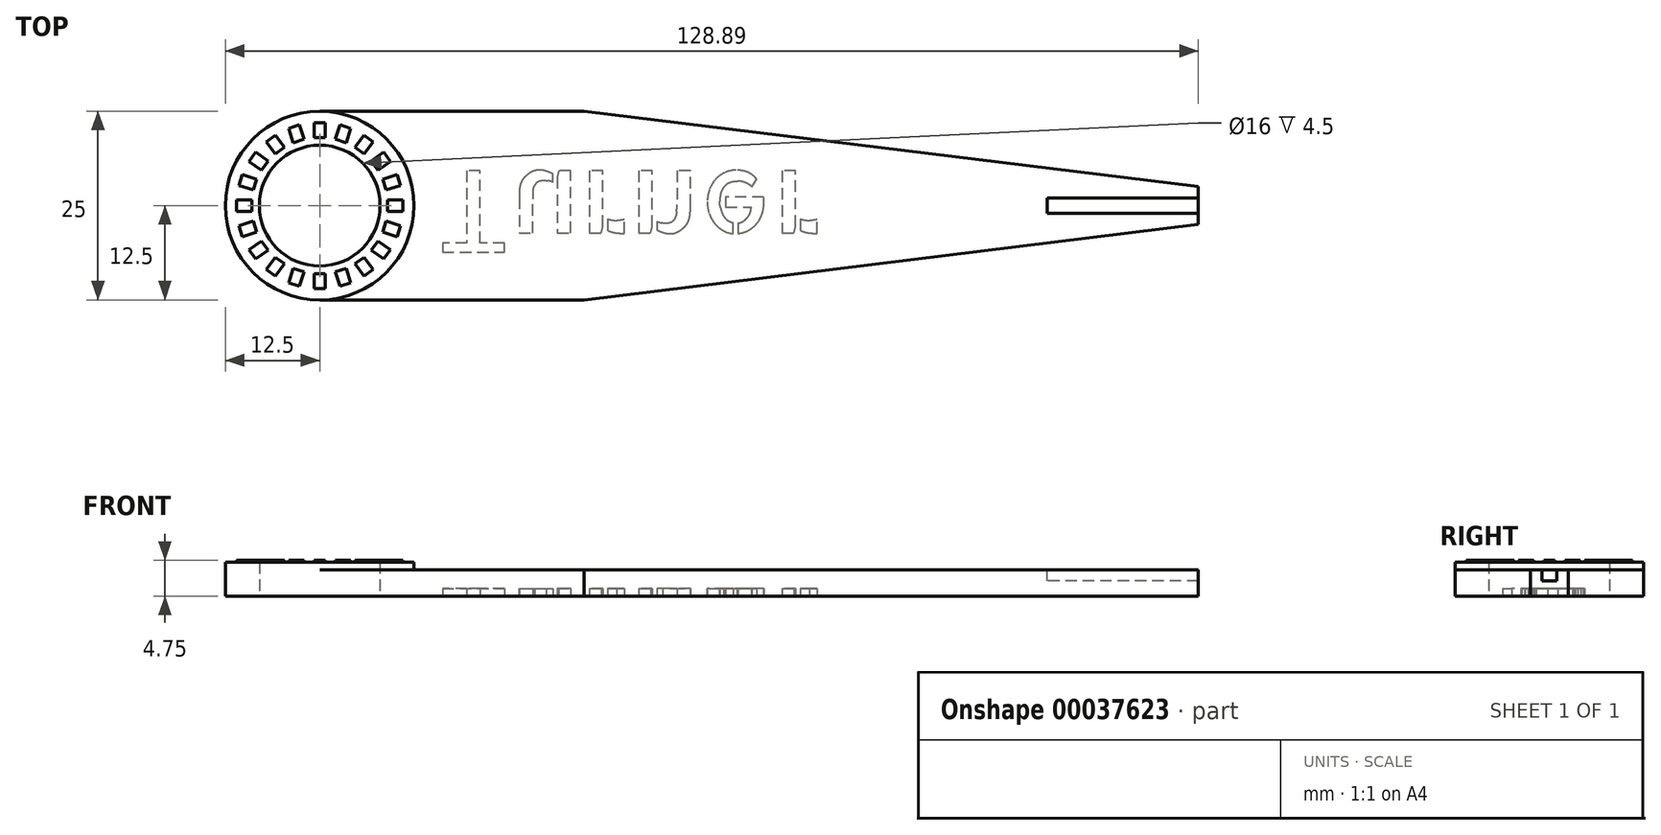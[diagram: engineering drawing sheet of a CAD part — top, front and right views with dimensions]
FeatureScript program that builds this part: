
annotation { "Feature Type Name" : "Feature", "Feature Type Description" : "" }
export const myFeature = defineFeature(function(context is Context, id is Id, definition is map)
    precondition{}
    {
        {
            var Q0;
            Q0=qCreatedBy(makeId("Top.planeOp"),FACE);
            var sketch = newSketch(context, id + "F0", { "sketchPlane" : qUnion([Q0])});
            skCircle(sketch, "E0", {"center": v(0, 0) * mm, "radius": 8 * mm});
            skCircle(sketch, "E1", {"center": v(0, 0) * mm, "radius": 12.5 * mm});
            skLineSegment(sketch, "E2", {"start": v(0, 12.5) * mm, "end": v(35, 12.5) * mm});
            skPoint(sketch, "E3", {"position": v(0, 12.5) * mm});
            skLineSegment(sketch, "E4", {"start": v(0, 0) * mm, "end": v(40.63, 0) * mm, "construction": true});
            skLineSegment(sketch, "E5.MirrorCS", {"start": v(0, -12.5) * mm, "end": v(35, -12.5) * mm});
            skLineSegment(sketch, "E6", {"start": v(35, 12.5) * mm, "end": v(108.8, 12.5) * mm, "construction": true});
            skLineSegment(sketch, "E7", {"start": v(35, 12.5) * mm, "end": v(116.39, 2.5) * mm});
            skLineSegment(sketch, "E8.MirrorCS", {"start": v(35, -12.5) * mm, "end": v(116.39, -2.5) * mm});
            skLineSegment(sketch, "E9", {"start": v(116.39, 2.5) * mm, "end": v(116.39, -2.5) * mm});
            skSolve(sketch);
        }
        {
            var Q0;
            Q0 = qSketchRegion(id + "F0", true);
            extrude(context, id + "F1", {"entities" : qUnion([Q0]), "depth" : 3.5 * mm});
        }
        {
            var Q0;
            Q0=makeQuery(id+"F1.opExtrude","CAP_FACE",FACE,{"disambiguationData":[OSD([sQuery(id+"F0.wireOp",EDGE,"E0"),sQuery(id+"F0.wireOp",EDGE,"E1"),sQuery(id+"F0.wireOp",EDGE,"E2"),sQuery(id+"F0.wireOp",EDGE,"E5.MirrorCS"),sQuery(id+"F0.wireOp",EDGE,"E7"),sQuery(id+"F0.wireOp",EDGE,"E8.MirrorCS"),sQuery(id+"F0.wireOp",EDGE,"E9")])],"isStart":false});
            var sketch = newSketch(context, id + "F2", { "sketchPlane" : qUnion([Q0])});
            skCircle(sketch, "E10", {"center": v(0, 0) * mm, "radius": 12.5 * mm});
            skCircle(sketch, "E11", {"center": v(0, 0) * mm, "radius": 8 * mm});
            skSolve(sketch);
        }
        {
            var Q0;
            Q0 = qSketchRegion(id + "F2", true);
            extrude(context, id + "F3", {"entities" : qUnion([Q0]), "operationType" : NewBodyOperationType.ADD, "depth" : 1 * mm});
        }
        {
            var Q0;
            Q0=makeQuery(id+"F3.opExtrude","CAP_FACE",FACE,{"disambiguationData":[OSD([sQuery(id+"F2.wireOp",EDGE,"E10"),sQuery(id+"F2.wireOp",EDGE,"E11")])],"isStart":false});
            var sketch = newSketch(context, id + "F4", { "sketchPlane" : qUnion([Q0])});
            skLineSegment(sketch, "E12.bottom", {"start": v(-0.75, 11) * mm, "end": v(0.75, 11) * mm});
            skLineSegment(sketch, "E12.top", {"start": v(-0.75, 9) * mm, "end": v(0.75, 9) * mm});
            skLineSegment(sketch, "E12.left", {"start": v(-0.75, 11) * mm, "end": v(-0.75, 9) * mm});
            skLineSegment(sketch, "E12.right", {"start": v(0.75, 11) * mm, "end": v(0.75, 9) * mm});
            skPoint(sketch, "E13", {"position": v(0, 8) * mm});
            skLineSegment(sketch, "E14.1.0", {"start": v(-4.11, 10.23) * mm, "end": v(-2.69, 10.7) * mm});
            skLineSegment(sketch, "E14.1.1", {"start": v(-4.11, 10.23) * mm, "end": v(-3.5, 8.33) * mm});
            skLineSegment(sketch, "E14.1.2", {"start": v(-3.5, 8.33) * mm, "end": v(-2.07, 8.8) * mm});
            skLineSegment(sketch, "E14.1.3", {"start": v(-2.69, 10.7) * mm, "end": v(-2.07, 8.8) * mm});
            skLineSegment(sketch, "E14.2.0", {"start": v(-7.07, 8.46) * mm, "end": v(-5.86, 9.34) * mm});
            skLineSegment(sketch, "E14.2.1", {"start": v(-7.07, 8.46) * mm, "end": v(-5.9, 6.84) * mm});
            skLineSegment(sketch, "E14.2.2", {"start": v(-5.9, 6.84) * mm, "end": v(-4.68, 7.72) * mm});
            skLineSegment(sketch, "E14.2.3", {"start": v(-5.86, 9.34) * mm, "end": v(-4.68, 7.72) * mm});
            skLineSegment(sketch, "E14.3.0", {"start": v(-9.34, 5.86) * mm, "end": v(-8.46, 7.07) * mm});
            skLineSegment(sketch, "E14.3.1", {"start": v(-9.34, 5.86) * mm, "end": v(-7.72, 4.68) * mm});
            skLineSegment(sketch, "E14.3.2", {"start": v(-7.72, 4.68) * mm, "end": v(-6.84, 5.9) * mm});
            skLineSegment(sketch, "E14.3.3", {"start": v(-8.46, 7.07) * mm, "end": v(-6.84, 5.9) * mm});
            skLineSegment(sketch, "E14.4.0", {"start": v(-10.7, 2.69) * mm, "end": v(-10.23, 4.11) * mm});
            skLineSegment(sketch, "E14.4.1", {"start": v(-10.7, 2.69) * mm, "end": v(-8.8, 2.07) * mm});
            skLineSegment(sketch, "E14.4.2", {"start": v(-8.8, 2.07) * mm, "end": v(-8.33, 3.5) * mm});
            skLineSegment(sketch, "E14.4.3", {"start": v(-10.23, 4.11) * mm, "end": v(-8.33, 3.5) * mm});
            skLineSegment(sketch, "E14.5.0", {"start": v(-11, -0.75) * mm, "end": v(-11, 0.75) * mm});
            skLineSegment(sketch, "E14.5.1", {"start": v(-11, -0.75) * mm, "end": v(-9, -0.75) * mm});
            skLineSegment(sketch, "E14.5.2", {"start": v(-9, -0.75) * mm, "end": v(-9, 0.75) * mm});
            skLineSegment(sketch, "E14.5.3", {"start": v(-11, 0.75) * mm, "end": v(-9, 0.75) * mm});
            skLineSegment(sketch, "E14.6.0", {"start": v(-10.23, -4.11) * mm, "end": v(-10.7, -2.69) * mm});
            skLineSegment(sketch, "E14.6.1", {"start": v(-10.23, -4.11) * mm, "end": v(-8.33, -3.5) * mm});
            skLineSegment(sketch, "E14.6.2", {"start": v(-8.33, -3.5) * mm, "end": v(-8.8, -2.07) * mm});
            skLineSegment(sketch, "E14.6.3", {"start": v(-10.7, -2.69) * mm, "end": v(-8.8, -2.07) * mm});
            skLineSegment(sketch, "E14.7.0", {"start": v(-8.46, -7.07) * mm, "end": v(-9.34, -5.86) * mm});
            skLineSegment(sketch, "E14.7.1", {"start": v(-8.46, -7.07) * mm, "end": v(-6.84, -5.9) * mm});
            skLineSegment(sketch, "E14.7.2", {"start": v(-6.84, -5.9) * mm, "end": v(-7.72, -4.68) * mm});
            skLineSegment(sketch, "E14.7.3", {"start": v(-9.34, -5.86) * mm, "end": v(-7.72, -4.68) * mm});
            skLineSegment(sketch, "E14.8.0", {"start": v(-5.86, -9.34) * mm, "end": v(-7.07, -8.46) * mm});
            skLineSegment(sketch, "E14.8.1", {"start": v(-5.86, -9.34) * mm, "end": v(-4.68, -7.72) * mm});
            skLineSegment(sketch, "E14.8.2", {"start": v(-4.68, -7.72) * mm, "end": v(-5.9, -6.84) * mm});
            skLineSegment(sketch, "E14.8.3", {"start": v(-7.07, -8.46) * mm, "end": v(-5.9, -6.84) * mm});
            skLineSegment(sketch, "E14.9.0", {"start": v(-2.69, -10.7) * mm, "end": v(-4.11, -10.23) * mm});
            skLineSegment(sketch, "E14.9.1", {"start": v(-2.69, -10.7) * mm, "end": v(-2.07, -8.8) * mm});
            skLineSegment(sketch, "E14.9.2", {"start": v(-2.07, -8.8) * mm, "end": v(-3.5, -8.33) * mm});
            skLineSegment(sketch, "E14.9.3", {"start": v(-4.11, -10.23) * mm, "end": v(-3.5, -8.33) * mm});
            skLineSegment(sketch, "E14.10.0", {"start": v(0.75, -11) * mm, "end": v(-0.75, -11) * mm});
            skLineSegment(sketch, "E14.10.1", {"start": v(0.75, -11) * mm, "end": v(0.75, -9) * mm});
            skLineSegment(sketch, "E14.10.2", {"start": v(0.75, -9) * mm, "end": v(-0.75, -9) * mm});
            skLineSegment(sketch, "E14.10.3", {"start": v(-0.75, -11) * mm, "end": v(-0.75, -9) * mm});
            skLineSegment(sketch, "E14.11.0", {"start": v(4.11, -10.23) * mm, "end": v(2.69, -10.7) * mm});
            skLineSegment(sketch, "E14.11.1", {"start": v(4.11, -10.23) * mm, "end": v(3.5, -8.33) * mm});
            skLineSegment(sketch, "E14.11.2", {"start": v(3.5, -8.33) * mm, "end": v(2.07, -8.8) * mm});
            skLineSegment(sketch, "E14.11.3", {"start": v(2.69, -10.7) * mm, "end": v(2.07, -8.8) * mm});
            skLineSegment(sketch, "E14.12.0", {"start": v(7.07, -8.46) * mm, "end": v(5.86, -9.34) * mm});
            skLineSegment(sketch, "E14.12.1", {"start": v(7.07, -8.46) * mm, "end": v(5.9, -6.84) * mm});
            skLineSegment(sketch, "E14.12.2", {"start": v(5.9, -6.84) * mm, "end": v(4.68, -7.72) * mm});
            skLineSegment(sketch, "E14.12.3", {"start": v(5.86, -9.34) * mm, "end": v(4.68, -7.72) * mm});
            skLineSegment(sketch, "E14.13.0", {"start": v(9.34, -5.86) * mm, "end": v(8.46, -7.07) * mm});
            skLineSegment(sketch, "E14.13.1", {"start": v(9.34, -5.86) * mm, "end": v(7.72, -4.68) * mm});
            skLineSegment(sketch, "E14.13.2", {"start": v(7.72, -4.68) * mm, "end": v(6.84, -5.9) * mm});
            skLineSegment(sketch, "E14.13.3", {"start": v(8.46, -7.07) * mm, "end": v(6.84, -5.9) * mm});
            skLineSegment(sketch, "E14.14.0", {"start": v(10.7, -2.69) * mm, "end": v(10.23, -4.11) * mm});
            skLineSegment(sketch, "E14.14.1", {"start": v(10.7, -2.69) * mm, "end": v(8.8, -2.07) * mm});
            skLineSegment(sketch, "E14.14.2", {"start": v(8.8, -2.07) * mm, "end": v(8.33, -3.5) * mm});
            skLineSegment(sketch, "E14.14.3", {"start": v(10.23, -4.11) * mm, "end": v(8.33, -3.5) * mm});
            skLineSegment(sketch, "E14.15.0", {"start": v(11, 0.75) * mm, "end": v(11, -0.75) * mm});
            skLineSegment(sketch, "E14.15.1", {"start": v(11, 0.75) * mm, "end": v(9, 0.75) * mm});
            skLineSegment(sketch, "E14.15.2", {"start": v(9, 0.75) * mm, "end": v(9, -0.75) * mm});
            skLineSegment(sketch, "E14.15.3", {"start": v(11, -0.75) * mm, "end": v(9, -0.75) * mm});
            skLineSegment(sketch, "E14.16.0", {"start": v(10.23, 4.11) * mm, "end": v(10.7, 2.69) * mm});
            skLineSegment(sketch, "E14.16.1", {"start": v(10.23, 4.11) * mm, "end": v(8.33, 3.5) * mm});
            skLineSegment(sketch, "E14.16.2", {"start": v(8.33, 3.5) * mm, "end": v(8.8, 2.07) * mm});
            skLineSegment(sketch, "E14.16.3", {"start": v(10.7, 2.69) * mm, "end": v(8.8, 2.07) * mm});
            skLineSegment(sketch, "E14.17.0", {"start": v(8.46, 7.07) * mm, "end": v(9.34, 5.86) * mm});
            skLineSegment(sketch, "E14.17.1", {"start": v(8.46, 7.07) * mm, "end": v(6.84, 5.9) * mm});
            skLineSegment(sketch, "E14.17.2", {"start": v(6.84, 5.9) * mm, "end": v(7.72, 4.68) * mm});
            skLineSegment(sketch, "E14.17.3", {"start": v(9.34, 5.86) * mm, "end": v(7.72, 4.68) * mm});
            skLineSegment(sketch, "E14.18.0", {"start": v(5.86, 9.34) * mm, "end": v(7.07, 8.46) * mm});
            skLineSegment(sketch, "E14.18.1", {"start": v(5.86, 9.34) * mm, "end": v(4.68, 7.72) * mm});
            skLineSegment(sketch, "E14.18.2", {"start": v(4.68, 7.72) * mm, "end": v(5.9, 6.84) * mm});
            skLineSegment(sketch, "E14.18.3", {"start": v(7.07, 8.46) * mm, "end": v(5.9, 6.84) * mm});
            skLineSegment(sketch, "E14.19.0", {"start": v(2.69, 10.7) * mm, "end": v(4.11, 10.23) * mm});
            skLineSegment(sketch, "E14.19.1", {"start": v(2.69, 10.7) * mm, "end": v(2.07, 8.8) * mm});
            skLineSegment(sketch, "E14.19.2", {"start": v(2.07, 8.8) * mm, "end": v(3.5, 8.33) * mm});
            skLineSegment(sketch, "E14.19.3", {"start": v(4.11, 10.23) * mm, "end": v(3.5, 8.33) * mm});
            skPoint(sketch, "E14.center", {"position": v(0, 0) * mm});
            skSolve(sketch);
        }
        {
            var Q0;
            Q0 = qSketchRegion(id + "F4", true);
            extrude(context, id + "F5", {"entities" : qUnion([Q0]), "operationType" : NewBodyOperationType.ADD, "depth" : .25 * mm});
        }
        {
            var Q0;
            Q0=makeQuery(id+"F1.opExtrude","CAP_FACE",FACE,{"disambiguationData":[OSD([sQuery(id+"F0.wireOp",EDGE,"E0"),sQuery(id+"F0.wireOp",EDGE,"E1"),sQuery(id+"F0.wireOp",EDGE,"E2"),sQuery(id+"F0.wireOp",EDGE,"E5.MirrorCS"),sQuery(id+"F0.wireOp",EDGE,"E7"),sQuery(id+"F0.wireOp",EDGE,"E8.MirrorCS"),sQuery(id+"F0.wireOp",EDGE,"E9")])],"isStart":false});
            var sketch = newSketch(context, id + "F6", { "sketchPlane" : qUnion([Q0])});
            skLineSegment(sketch, "E15.bottom", {"start": v(116.39, 1) * mm, "end": v(96.39, 1) * mm});
            skLineSegment(sketch, "E15.top", {"start": v(116.39, -1) * mm, "end": v(96.39, -1) * mm});
            skLineSegment(sketch, "E15.left", {"start": v(116.39, 1) * mm, "end": v(116.39, -1) * mm});
            skLineSegment(sketch, "E15.right", {"start": v(96.39, 1) * mm, "end": v(96.39, -1) * mm});
            skSolve(sketch);
        }
        {
            var Q0;
            Q0=makeQuery(id+"F1.opExtrude","CAP_FACE",FACE,{"disambiguationData":[OSD([sQuery(id+"F0.wireOp",EDGE,"E0"),sQuery(id+"F0.wireOp",EDGE,"E1"),sQuery(id+"F0.wireOp",EDGE,"E2"),sQuery(id+"F0.wireOp",EDGE,"E5.MirrorCS"),sQuery(id+"F0.wireOp",EDGE,"E7"),sQuery(id+"F0.wireOp",EDGE,"E8.MirrorCS"),sQuery(id+"F0.wireOp",EDGE,"E9")])],"isStart":true});
            var sketch = newSketch(context, id + "F7", { "sketchPlane" : qUnion([Q0])});
            skText(sketch, "E16", { "text": "Turner", "fontName": "AllertaStencil-Regular.ttf"});
            const initialGuessF7  = {"E16": [0.01552, -0.00463, 1, 0, 0.01079]};
            skSetInitialGuess(sketch, initialGuessF7);
            skSolve(sketch);
        }
        {
            var Q0;
            Q0 = qSketchRegion(id + "F7", true);
            extrude(context, id + "F8", {"entities" : qUnion([Q0]), "operationType" : NewBodyOperationType.REMOVE, "oppositeDirection" : true, "depth" : 1 * mm});
        }
        {
            var Q0;
            Q0 = qSketchRegion(id + "F6", true);
            extrude(context, id + "F9", {"entities" : qUnion([Q0]), "operationType" : NewBodyOperationType.REMOVE, "oppositeDirection" : true, "depth" : 1.5 * mm});
        }
    });
